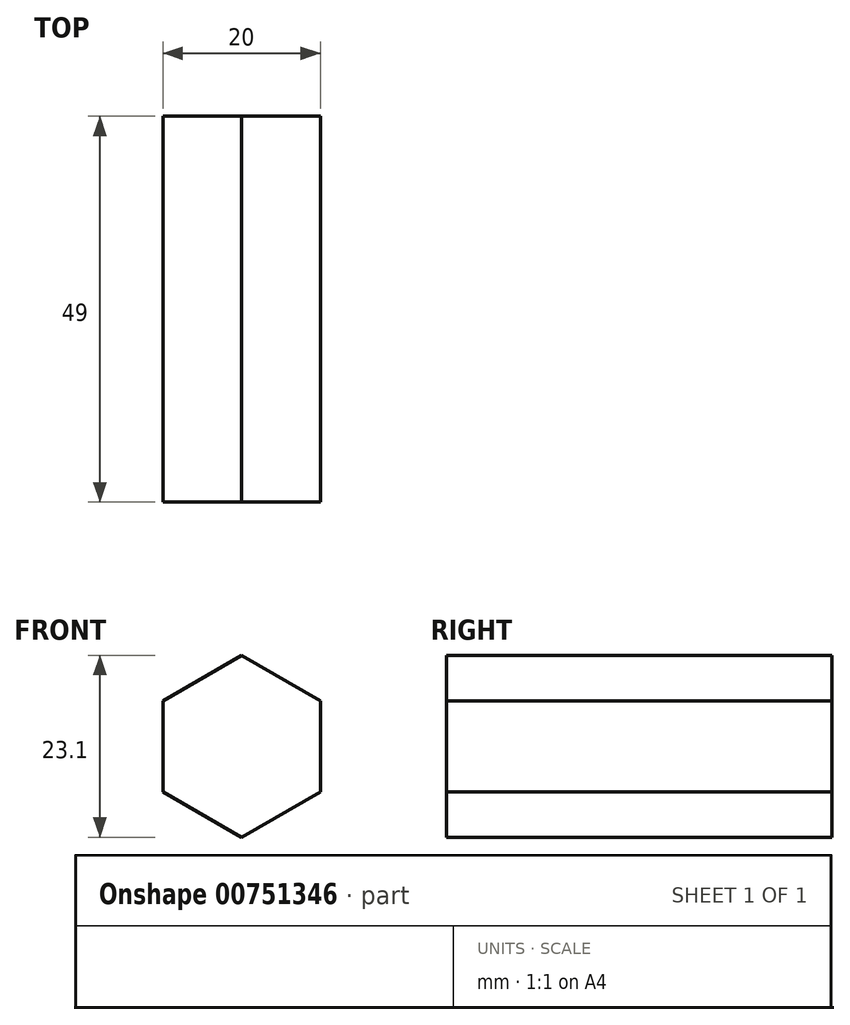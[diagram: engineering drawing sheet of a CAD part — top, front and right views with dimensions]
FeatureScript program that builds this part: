
annotation { "Feature Type Name" : "Feature", "Feature Type Description" : "" }
export const myFeature = defineFeature(function(context is Context, id is Id, definition is map)
    precondition{}
    {
        {
            var Q0;
            Q0=qCreatedBy(makeId("Front.planeOp"),FACE);
            var sketch = newSketch(context, id + "F0", { "sketchPlane" : qUnion([Q0])});
            skCircle(sketch, "E0", {"center": v(0, 0) * mm, "radius": 10 * mm});
            skCircle(sketch, "E1.cCircle", {"center": v(0, 0) * mm, "radius": 10 * mm, "construction": true});
            skLineSegment(sketch, "E1.0", {"start": v(-10, -5.77) * mm, "end": v(-10, 5.77) * mm});
            skLineSegment(sketch, "E1.1", {"start": v(-10, 5.77) * mm, "end": v(0, 11.55) * mm});
            skLineSegment(sketch, "E1.2", {"start": v(0, 11.55) * mm, "end": v(10, 5.77) * mm});
            skLineSegment(sketch, "E1.3", {"start": v(10, 5.77) * mm, "end": v(10, -5.77) * mm});
            skLineSegment(sketch, "E1.4", {"start": v(10, -5.77) * mm, "end": v(0, -11.55) * mm});
            skLineSegment(sketch, "E1.5", {"start": v(0, -11.55) * mm, "end": v(-10, -5.77) * mm});
            skPoint(sketch, "E1.0.midPoint", {"position": v(-10, 0) * mm});
            skSolve(sketch);
        }
        {
            var Q0;
            Q0 = qSketchRegion(id + "F0", true);
            extrude(context, id + "F1", {"entities" : qUnion([Q0]), "endBound" : BoundingType.SYMMETRIC, "depth" : 49 * mm, "offsetDistance" : 25 * mm});
        }
    });
